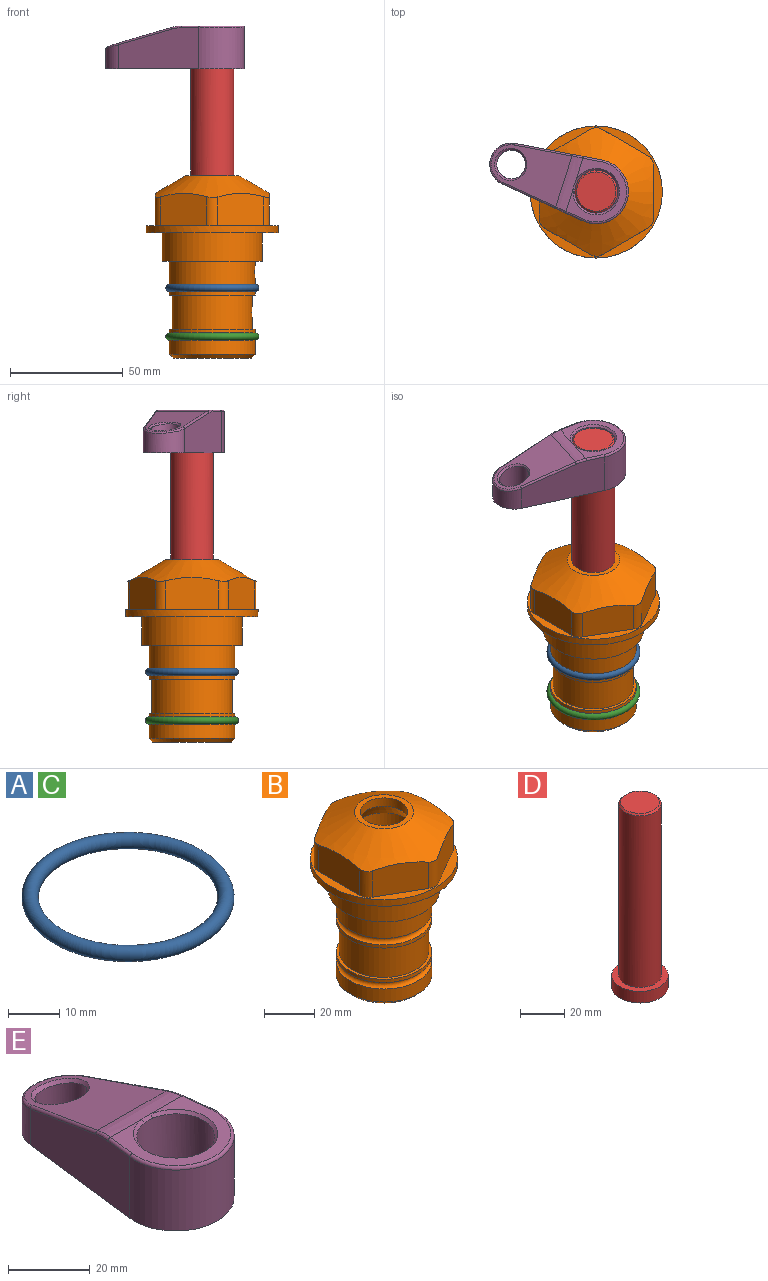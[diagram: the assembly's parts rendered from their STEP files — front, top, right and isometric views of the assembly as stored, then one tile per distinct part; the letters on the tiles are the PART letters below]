
ASSEMBLY  parts=5 mates=4
PART A: 1 faces, bbox 44.7x44.7x3.2 mm
  f0: torus R=19.05mm, axis (0,0,1), area 1193.9mm2
PART B: 36 faces, bbox 58.7x58.7x81 mm
  f0: cylinder r=17.78mm len=35.56mm, axis (0,0,1), area 1670.8mm2, adj f23,f24,f31
  f1: cylinder r=19.05mm len=38.1mm, axis (0,0,1), area 1191.9mm2, adj f26,f27,f30
  f2: plane 58.66x58.66mm, normal (0,0,-1), area 1150.6mm2, adj f3,f28
  f3: cylinder r=29.33mm len=58.66mm, axis (0,0,-1), area 585.1mm2, adj f2,f4
  f4: plane 58.66x58.66mm, normal (0,0,1), area 475.9mm2, adj f3,f5,f6,f7,f8,f9,f10,f11
  f5: plane 20.32x14.34mm, normal (-0.5,0.87,0), area 324.4mm2, adj f4,f15,f16,f17
  f6: plane 20.32x14.34mm, normal (0.5,0.87,0), area 324.4mm2, adj f4,f14,f15,f17
  f7: plane 23.48x14.34mm, normal (1,0,0), area 324.4mm2, adj f4,f13,f14,f17
  f8: plane 20.32x14.34mm, normal (0.5,-0.87,0), area 324.4mm2, adj f4,f12,f13,f17
  f9: plane 20.32x14.34mm, normal (-0.5,-0.87,0), area 324.4mm2, adj f4,f11,f12,f17
  f10: plane 23.48x14.34mm, normal (-1,0,0), area 324.4mm2, adj f4,f11,f16,f17
  f11: cylinder r=5.08mm len=12.85mm, axis (0,0,-1), area 67.2mm2, adj f4,f9,f10,f17
  f12: cylinder r=5.08mm len=12.85mm, axis (0,0,-1), area 67.2mm2, adj f4,f8,f9,f17
  f13: cylinder r=5.08mm len=12.85mm, axis (0,0,-1), area 67.2mm2, adj f4,f7,f8,f17
  f14: cylinder r=5.08mm len=12.85mm, axis (0,0,-1), area 67.2mm2, adj f4,f6,f7,f17
  f15: cylinder r=5.08mm len=12.85mm, axis (0,0,-1), area 67.2mm2, adj f4,f5,f6,f17
  f16: cylinder r=5.08mm len=12.85mm, axis (0,0,-1), area 67.2mm2, adj f4,f5,f10,f17
  f17: cone r=11.73mm half-angle=60deg, axis (0,0,-1), area 2071.8mm2, adj f5,f6,f7,f8,f9,f10,f11,f12
  f18: plane 23.46x23.46mm, normal (0,0,1), area 147.4mm2, adj f17,f35
  f19: plane 34.93x34.93mm, normal (0,0,-1), area 958mm2, adj f29
  f20: cylinder r=19.05mm len=38.1mm, axis (0,0,1), area 760.1mm2, adj f21,f29
  f21: torus R=19.05mm, axis (0,0,1), area 565.3mm2, adj f20,f22
  f22: cylinder r=19.05mm len=38.1mm, axis (0,0,1), area 190mm2, adj f21,f23
  f23: plane 38.1x38.1mm, normal (0,0,1), area 146.9mm2, adj f0,f22
  f24: plane 38.1x38.1mm, normal (0,0,-1), area 146.9mm2, adj f0,f25
  f25: cylinder r=19.05mm len=38.1mm, axis (0,0,1), area 190mm2, adj f24,f26
  f26: torus R=19.05mm, axis (0,0,1), area 565.3mm2, adj f1,f25
  f27: plane 44.45x44.45mm, normal (0,0,-1), area 411.7mm2, adj f1,f28
  f28: cylinder r=22.23mm len=44.45mm, axis (0,0,1), area 1773.5mm2, adj f2,f27
  f29: cone r=19.05mm half-angle=45deg, axis (0,0,1), area 257.5mm2, adj f19,f20
  f30: cylinder r=3.17mm len=6.75mm, axis (-1,0,0), area 128mm2, adj f1,f33
  f31: cylinder r=3.17mm len=6.35mm, axis (-1,0,0), area 102.5mm2, adj f0,f33
  f32: plane 25.4x25.4mm, normal (0,0,1), area 506.7mm2, adj f33
  f33: cylinder r=12.7mm len=66.42mm, axis (0,0,-1), area 5236.2mm2, adj f30,f31,f32,f34
  f34: cone r=9.53mm half-angle=30deg, axis (0,0,-1), area 443.4mm2, adj f33,f35
  f35: cylinder r=9.53mm len=19.05mm, axis (0,0,-1), area 240.9mm2, adj f18,f34
PART C: same geometry as A
PART D: 6 faces, bbox 25.4x25.4x101.6 mm
  f0: plane 17.46x17.46mm, normal (0,0,1), area 239.5mm2, adj f5
  f1: plane 25.4x25.4mm, normal (0,0,-1), area 506.7mm2, adj f2
  f2: cylinder r=12.7mm len=25.4mm, axis (0,0,1), area 506.7mm2, adj f1,f3
  f3: plane 25.4x25.4mm, normal (0,0,1), area 221.7mm2, adj f2,f4
  f4: cylinder r=9.53mm len=94.46mm, axis (0,0,1), area 5653mm2, adj f3,f5
  f5: cone r=8.73mm half-angle=45deg, axis (0,0,-1), area 64.4mm2, adj f0,f4
PART E: 31 faces, bbox 31.7x65.5x19.8 mm
  f0: plane 39.12x18.26mm, normal (0.99,0.12,0), area 612.2mm2, adj f1,f4,f7,f11,f13,f15
  f1: cylinder r=9.53mm len=18.91mm, axis (0,0,-1), area 296.1mm2, adj f0,f2,f7,f17
  f2: plane 39.12x18.26mm, normal (-0.99,0.12,0), area 612.2mm2, adj f1,f4,f7,f12,f14,f16
  f3: cylinder r=6.35mm len=12.7mm, axis (0,0,-1), area 362.4mm2, adj f7,f18
  f4: cylinder r=14.29mm len=28.58mm, axis (0,0,-1), area 882.2mm2, adj f0,f2,f7,f10
  f5: cylinder r=9.53mm len=19.05mm, axis (0,0,-1), area 1092.6mm2, adj f7,f19,f20
  f6: plane 26.99x23.69mm, normal (0,0,1), area 216.2mm2, adj f9,f10,f11,f12,f19
  f7: plane 63.5x28.58mm, normal (0,0,-1), area 661.8mm2, adj f0,f1,f2,f3,f4,f5,f22,f23
  f8: plane 33.52x23.6mm, normal (0,0.26,0.97), area 486mm2, adj f9,f15,f16,f17,f18
  f9: cylinder r=19.05mm len=24.72mm, axis (1,0,0), area 120.4mm2, adj f6,f8,f13,f14,f20
  f10: torus R=13.49mm, axis (0,0,1), area 59mm2, adj f4,f6,f11,f12
  f11: cylinder r=0.79mm len=8.67mm, axis (0.12,-0.99,0), area 10.8mm2, adj f0,f6,f10,f13
  f12: cylinder r=0.79mm len=8.67mm, axis (0.12,0.99,0), area 10.8mm2, adj f2,f6,f10,f14
  f13: bspline ~4.95x1.42mm, area 6.1mm2, adj f0,f9,f11,f15
  f14: bspline ~4.95x1.42mm, area 6.1mm2, adj f2,f9,f12,f16
  f15: cylinder r=0.79mm len=25.95mm, axis (0.12,-0.96,0.26), area 32.9mm2, adj f0,f8,f13,f17
  f16: cylinder r=0.79mm len=25.95mm, axis (0.12,0.96,-0.26), area 32.9mm2, adj f2,f8,f14,f17
  f17: bspline ~18.91x8.38mm, area 30mm2, adj f1,f8,f15,f16
  f18: bspline ~14.29x14.29mm, area 48.3mm2, adj f3,f8
  f19: cone r=9.53mm half-angle=45deg, axis (0,0,1), area 66.5mm2, adj f5,f6,f20
  f20: bspline ~3.22x0.96mm, area 3.5mm2, adj f5,f9,f19
  f21: plane 2.75x2.72mm, normal (0,0,-1), area 2.9mm2, adj f23,f25,f28
  f22: plane 23.05x15.88mm, normal (-0.99,-0.12,0), area 323.6mm2, adj f7,f25,f26,f27,f28,f29
  f23: plane 23.05x15.88mm, normal (0.99,-0.12,0), area 323.6mm2, adj f7,f21,f25,f27,f28,f30
  f24: cylinder r=9.53mm len=10.69mm, axis (0,0,-1), area 114.7mm2, adj f7,f27,f29,f30
  f25: cylinder r=12.7mm len=20.59mm, axis (0,0,-1), area 381.1mm2, adj f7,f21,f22,f23,f26,f28
  f26: plane 2.75x2.72mm, normal (0,0,-1), area 2.9mm2, adj f22,f25,f28
  f27: plane 19.72x18.37mm, normal (0,-0.26,-0.97), area 291.8mm2, adj f22,f23,f24,f28,f29,f30
  f28: cylinder r=15.88mm len=19.92mm, axis (1,0,0), area 54.8mm2, adj f21,f22,f23,f25,f26,f27
  f29: cylinder r=1.59mm len=11mm, axis (0,0,-1), area 34.7mm2, adj f7,f22,f24,f27
  f30: cylinder r=1.59mm len=11mm, axis (0,0,-1), area 34.7mm2, adj f7,f23,f24,f27
PLACE A at identity
PLACE B at identity fixed
PLACE C t=(0,0,-21.59)mm
PLACE D rot(axis=(0,0,1),72.3deg) t=(0,0,27.55)mm
PLACE E rot(axis=(0,0,1),72.3deg) t=(0,0,28.35)mm
MATE fastened D.f2 <-> E.f4  axis (0,0,1) through (0,0,91.05)mm
MATE cylindrical B.f0 <-> D.f2  axis (0,0,1) through (0,0,-50.55)mm
MATE fastened C.f0 <-> B.f0  axis (0,0,1) through (0,0,-46.1)mm
MATE fastened A.f0 <-> B.f0  axis (0,0,1) through (0,0,-24.51)mm
